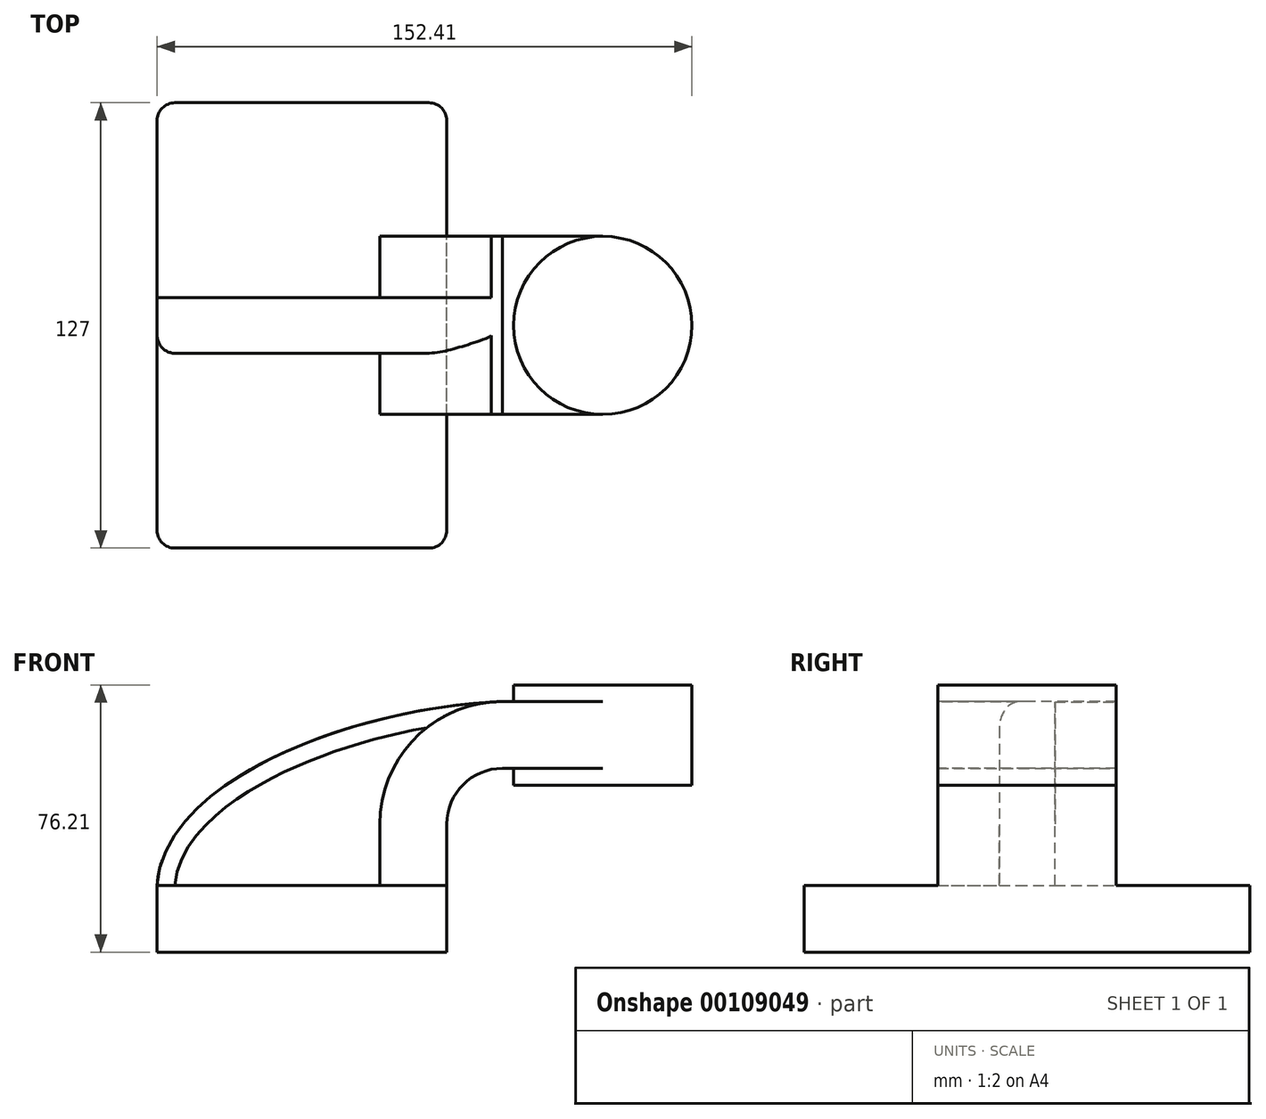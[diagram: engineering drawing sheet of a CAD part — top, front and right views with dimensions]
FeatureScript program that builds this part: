
annotation { "Feature Type Name" : "Feature", "Feature Type Description" : "" }
export const myFeature = defineFeature(function(context is Context, id is Id, definition is map)
    precondition{}
    {
        {
            var Q0;
            Q0=qCreatedBy(makeId("Front.planeOp"),FACE);
            var sketch = newSketch(context, id + "F0", { "sketchPlane" : qUnion([Q0])});
            skLineSegment(sketch, "E0.rect.bottom", {"start": v(-41.28, 9.52) * mm, "end": v(41.28, 9.52) * mm});
            skLineSegment(sketch, "E0.rect.top", {"start": v(-41.28, -9.52) * mm, "end": v(41.28, -9.52) * mm});
            skLineSegment(sketch, "E0.rect.left", {"start": v(-41.28, 9.52) * mm, "end": v(-41.28, -9.52) * mm});
            skLineSegment(sketch, "E0.rect.right", {"start": v(41.28, 9.52) * mm, "end": v(41.28, -9.52) * mm});
            skPoint(sketch, "E0.rect.middle", {"position": v(0, 0) * mm});
            skLineSegment(sketch, "E1", {"start": v(41.28, 9.52) * mm, "end": v(41.28, 27) * mm});
            skArc(sketch, "E2", {"start": v(41.28, 27) * mm, "mid": v(45.92, 38.23) * mm, "end": v(57.15, 42.88) * mm});
            skLineSegment(sketch, "E3", {"start": v(57.15, 42.88) * mm, "end": v(85.72, 42.88) * mm});
            skLineSegment(sketch, "E4.rect.bottom", {"start": v(60.32, 38.1) * mm, "end": v(111.12, 38.1) * mm});
            skLineSegment(sketch, "E4.rect.top", {"start": v(60.32, 66.68) * mm, "end": v(111.12, 66.68) * mm});
            skLineSegment(sketch, "E4.rect.left", {"start": v(60.32, 38.1) * mm, "end": v(60.32, 66.68) * mm});
            skLineSegment(sketch, "E4.rect.right", {"start": v(111.13, 38.1) * mm, "end": v(111.12, 66.68) * mm});
            skPoint(sketch, "E4.rect.middle", {"position": v(85.72, 52.39) * mm});
            skLineSegment(sketch, "E5.0", {"start": v(57.15, 61.93) * mm, "end": v(85.72, 61.93) * mm});
            skArc(sketch, "E5.1", {"start": v(22.23, 27) * mm, "mid": v(32.45, 51.7) * mm, "end": v(57.15, 61.93) * mm});
            skLineSegment(sketch, "E5.2", {"start": v(22.23, 9.52) * mm, "end": v(22.23, 27) * mm});
            skLineSegment(sketch, "E6", {"start": v(85.72, 38.1) * mm, "end": v(85.72, 66.68) * mm});
            skFitSpline(sketch, "E7", {"points": [v(-41.28, 9.53) * mm, v(57.15, 61.93) * mm], "startDerivative": vector(5.2, 92.34) * mm, "endDerivative": vector(120.92, 4.22) * mm});
            skSolve(sketch);
        }
        {
            var Q0;
            Q0=makeQuery(id+"F0.imprint","IMPRINT",FACE,{"disambiguationData":[TD([[makeQuery(id+"F0.imprint","IMPRINT",EDGE,{"derivedFrom":sQuery(id+"F0.wireOp",EDGE,"E0.rect.top")}),1.0]])]});
            extrude(context, id + "F1", {"entities" : qUnion([Q0]), "endBound" : BoundingType.SYMMETRIC, "depth" : 127 * mm});
        }
        {
            var Q0;
            {var subQ9=sQuery(id+"F0.wireOp",EDGE,"E1");Q0=makeQuery(id+"F0.imprint","IMPRINT",FACE,{"disambiguationData":[TD([[makeQuery(id+"F0.imprint","IMPRINT",EDGE,{"derivedFrom":subQ9}),1.0]])]});}
            var Q1;
            {var subQ0=sQuery(id+"F0.wireOp",EDGE,"E6");var subQ1=sQuery(id+"F0.wireOp",EDGE,"E3");var subQ2=makeQuery(id+"F0.imprint","INTERSECT",VERTEX,{"derivedFrom":[subQ1,subQ0]});Q1=makeQuery(id+"F0.imprint","IMPRINT",FACE,{"disambiguationData":[TD([[makeQuery(id+"F0.imprint","IMPRINT",EDGE,{"disambiguationData":[TD([[subQ2,1.0]])],"derivedFrom":subQ1}),1.0]])]});}
            extrude(context, id + "F2", {"entities" : qUnion([Q0, Q1]), "operationType" : NewBodyOperationType.ADD, "endBound" : BoundingType.SYMMETRIC, "depth" : 50.8 * mm});
        }
        {
            var Q0;
            {var subQ3=sQuery(id+"F0.wireOp",EDGE,"E5.2");Q0=makeQuery(id+"F0.imprint","IMPRINT",FACE,{"disambiguationData":[TD([[makeQuery(id+"F0.imprint","IMPRINT",EDGE,{"derivedFrom":subQ3}),1.0]])]});}
            extrude(context, id + "F3", {"entities" : qUnion([Q0]), "operationType" : NewBodyOperationType.ADD, "endBound" : BoundingType.SYMMETRIC, "depth" : 15.88 * mm});
        }
        {
            var Q0;
            {var subQ5=sQuery(id+"F0.wireOp",EDGE,"E4.rect.right");Q0=makeQuery(id+"F0.imprint","IMPRINT",FACE,{"disambiguationData":[TD([[makeQuery(id+"F0.imprint","IMPRINT",EDGE,{"derivedFrom":subQ5}),1.0]])]});}
            var Q1;
            Q1=sQuery(id+"F0.wireOp",EDGE,"E6");
            revolve(context, id + "F4", {"operationType" : NewBodyOperationType.ADD, "entities" : qUnion([Q0]), "axis" : qUnion([Q1]), "revolveType" : RevolveType.FULL});
        }
        {
            var Q0;
            Q0=makeQuery(id+"F1.opExtrude","CAP_EDGE",EDGE,{"disambiguationData":[OSD([sQuery(id+"F0.wireOp",EDGE,"E0.rect.right")])],"isStart":false});
            var Q1;
            Q1=makeQuery(id+"F1.opExtrude","CAP_EDGE",EDGE,{"disambiguationData":[OSD([sQuery(id+"F0.wireOp",EDGE,"E0.rect.left")])],"isStart":false});
            var Q2;
            Q2=makeQuery(id+"F1.opExtrude","CAP_EDGE",EDGE,{"disambiguationData":[OSD([sQuery(id+"F0.wireOp",EDGE,"E0.rect.right")])],"isStart":true});
            var Q3;
            Q3=makeQuery(id+"F1.opExtrude","CAP_EDGE",EDGE,{"disambiguationData":[OSD([sQuery(id+"F0.wireOp",EDGE,"E0.rect.left")])],"isStart":true});
            fillet(context, id + "F5", {"entities" : qUnion([Q0, Q1, Q2, Q3]), "radius" : 5.08 * mm, "tangentPropagation" : true, "allowEdgeOverflow" : false});
        }
        {
            var Q0;
            Q0=makeQuery(id+"F3.opExtrude","CAP_EDGE",EDGE,{"disambiguationData":[OSD([sQuery(id+"F0.wireOp",EDGE,"E7")])],"isStart":false});
            fillet(context, id + "F6", {"entities" : qUnion([Q0]), "radius" : 5.08 * mm, "tangentPropagation" : true, "allowEdgeOverflow" : false});
        }
    });
